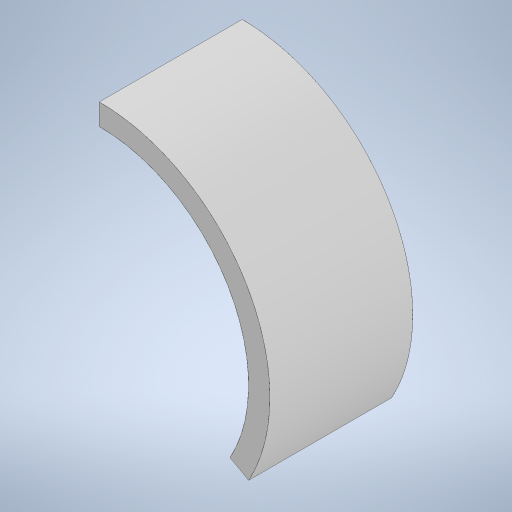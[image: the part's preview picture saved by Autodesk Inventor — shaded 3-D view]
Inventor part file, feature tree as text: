
AUTODESK INVENTOR PART (.ipt)
format: ipt  version: 2024 (Build 280153000, 153)  size: 338,944 bytes
history: native  units: mm
features: other x16, extrude x7, sketch x7, fillet x2
ambient origin geometry x8: Origin, YZ Plane, XZ Plane, XY Plane, X Axis, Y Axis, Z Axis, Center Point
bodies: Body1 (feature_tree)
feature tree (32):
  extrude  "Wyciągnięcie proste2"  Depth=30.0mm TaperAngle=360.0deg
  extrude  "Wyciągnięcie proste3"  Depth=2.0mm TaperAngle=0.0deg
  extrude  "Wyciągnięcie proste4"  Depth=12.0mm TaperAngle=0.0deg
  other  "Pogrubienie1"
  other  "Pogrubienie2"
  other  "Pogrubienie3"
  extrude  "Wyciągnięcie proste5"  Depth=1.0mm TaperAngle=0.0deg
  other  "Pogrubienie4"
  extrude  "Wyciągnięcie proste6"  Depth=0.1mm
  fillet  "Zaokrąglenie1"  Radius=0.1mm
  extrude  "Wyciągnięcie proste7"  Depth=0.1mm
  extrude  "Wyciągnięcie proste8"  Depth=0.1mm
  other  "Pogrubienie5"
  other  "Pogrubienie6"
  sketch  "Szkic6"
  sketch  "Szkic7"
  other  "Pogrubienie7"
  other  "Pogrubienie8"
  other  "Pogrubienie9"
  other  "Pogrubienie10"
  other  "Pogrubienie11"
  other  "Pogrubienie12"
  other  "Pogrubienie13"
  other  "Pogrubienie14"
  other  "Pogrubienie15"
  other  "Pogrubienie16"
  fillet  "Zaokrąglenie2"  Radius=0.1mm
  sketch  "Szkic2"
  sketch  "Szkic3"
  sketch  "Szkic4"
  sketch  "Szkic5"
  sketch  "Szkic1"
